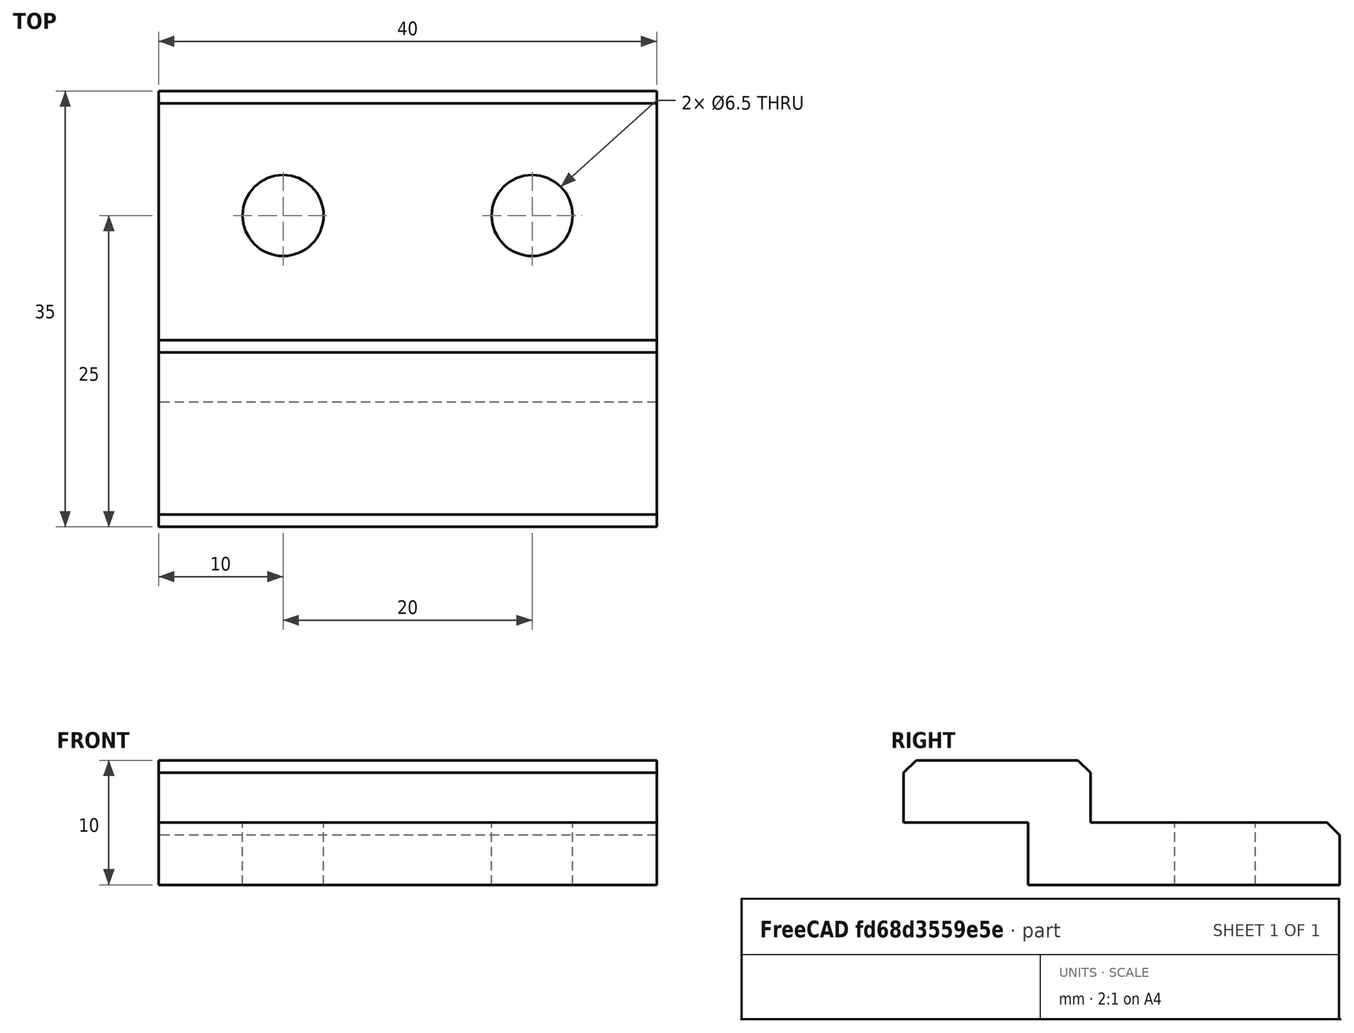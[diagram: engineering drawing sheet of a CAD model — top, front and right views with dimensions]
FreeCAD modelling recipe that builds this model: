
FCSTD DOCUMENT  (FreeCAD 0.14R3703 (Git))
Label: guia_cubeta_frontal_der
License: CC-BY 3.0
LicenseURL: http://creativecommons.org/licenses/by/3.0/
objects: Part::Chamfer×3, Part::Cylinder×2, Part::Box×2, Part::Cut×2, Part::Fuse×1, Part::Feature×1
note: 11 computed .brp shape members not serialized (recipe doc carries the construction recipe); baked Part::Feature solids carry a one-line shape summary decoded from their .brp

FEATURE [Part::Cylinder] Cylinder  label="Cilindro001"
  Angle = 360
  Height = 10
  Placement = pos=(30,10,0) rot=(0,0,1;0rad)
  Radius = 3.25
FEATURE [Part::Box] Box  label="Cubo001"
  Height = 5
  Length = 40
  Placement = pos=(0,20,5) rot=(0,0,1;0rad)
  Width = 15
FEATURE [Part::Box] Box001  label="Cubo"
  Height = 5
  Length = 40
  Width = 25
FEATURE [Part::Chamfer] Chamfer
  Base = -> Box
  Edges = 1 edges r=1: [Edge10]
FEATURE [Part::Chamfer] Chamfer001
  Base = -> Chamfer
  Edges = 1 edges r=1: [Edge13]
FEATURE [Part::Cylinder] Cylinder001  label="Cilindro"
  Angle = 360
  Height = 10
  Placement = pos=(10,10,0) rot=(0,0,1;0rad)
  Radius = 3.25
FEATURE [Part::Chamfer] Chamfer002
  Base = -> Box001
  Edges = 1 edges r=1: [Edge10]
FEATURE [Part::Fuse] Fusion
  Base = -> Chamfer002
  Tool = -> Chamfer001
FEATURE [Part::Cut] Cut001
  Base = -> Fusion
  Tool = -> Cylinder001
FEATURE [Part::Cut] Cut
  Base = -> Cut001
  Placement = pos=(0,35,0) rot=(0,0,1;3.14159rad)
  Tool = -> Cylinder
FEATURE [Part::Feature] Cut002  label="guia_cubeta_frontal_der"
  Placement = pos=(0,35,0) rot=(0,0,1;3.14159rad)
  shape: bbox 40 x 35 x 10 mm, 15 faces (baked)
